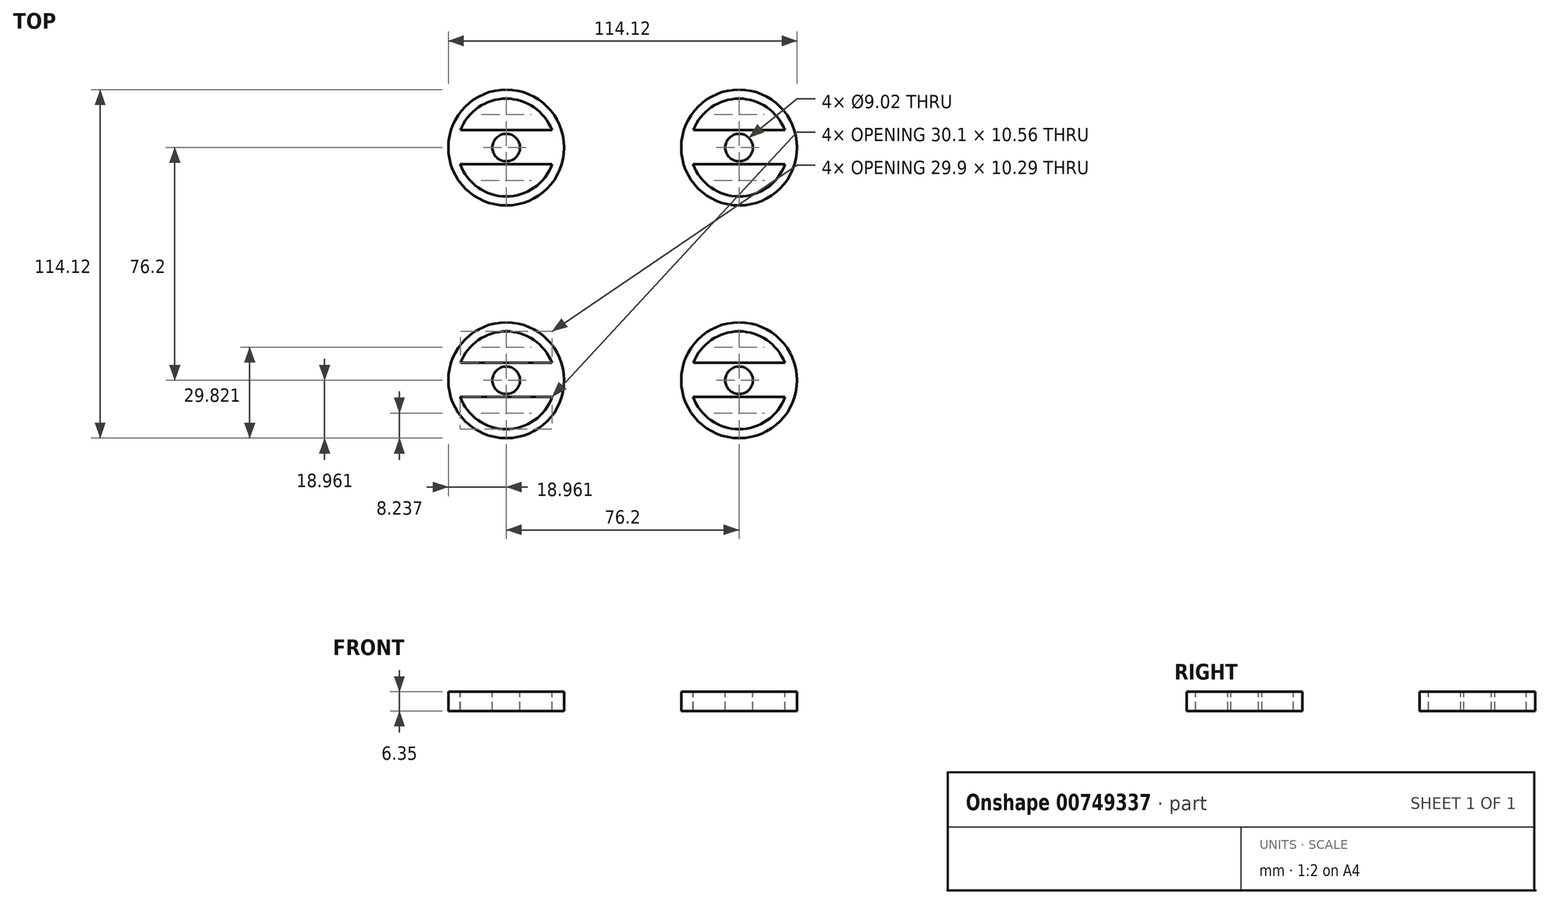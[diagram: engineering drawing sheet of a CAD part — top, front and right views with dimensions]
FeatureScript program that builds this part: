
annotation { "Feature Type Name" : "Feature", "Feature Type Description" : "" }
export const myFeature = defineFeature(function(context is Context, id is Id, definition is map)
    precondition{}
    {
        {
            var Q0;
            Q0=qCreatedBy(makeId("Top.planeOp"),FACE);
            var sketch = newSketch(context, id + "F0", { "sketchPlane" : qUnion([Q0])});
            skCircle(sketch, "E0", {"center": v(-43.12, 40.67) * mm, "radius": 18.96 * mm});
            skSolve(sketch);
        }
        {
            var Q0;
            Q0 = qSketchRegion(id + "F0", true);
            extrude(context, id + "F1", {"entities" : qUnion([Q0]), "depth" : 6.35 * mm, "offsetDistance" : 25.4 * mm});
        }
        {
            var Q0;
            Q0=makeQuery(id+"F1.opExtrude","CAP_FACE",FACE,{"disambiguationData":[OSD([sQuery(id+"F0.wireOp",EDGE,"E0")])],"isStart":false});
            var sketch = newSketch(context, id + "F2", { "sketchPlane" : qUnion([Q0])});
            skCircle(sketch, "E1", {"center": v(-43.12, 40.67) * mm, "radius": 16 * mm});
            skSolve(sketch);
        }
        {
            var Q0;
            Q0 = qSketchRegion(id + "F2", true);
            extrude(context, id + "F3", {"entities" : qUnion([Q0]), "operationType" : NewBodyOperationType.REMOVE, "oppositeDirection" : true, "depth" : 25.4 * mm, "offsetDistance" : 25.4 * mm});
        }
        {
            var Q0;
            Q0=makeQuery(id+"F1.opExtrude","CAP_FACE",FACE,{"disambiguationData":[OSD([sQuery(id+"F0.wireOp",EDGE,"E0")])],"isStart":false});
            var sketch = newSketch(context, id + "F4", { "sketchPlane" : qUnion([Q0])});
            skLineSegment(sketch, "E2.bottom", {"start": v(-60.69, 46.38) * mm, "end": v(-25.18, 46.38) * mm});
            skLineSegment(sketch, "E2.top", {"start": v(-60.69, 35.23) * mm, "end": v(-25.18, 35.23) * mm});
            skLineSegment(sketch, "E2.left", {"start": v(-60.69, 46.38) * mm, "end": v(-60.69, 35.23) * mm});
            skLineSegment(sketch, "E2.right", {"start": v(-25.18, 46.38) * mm, "end": v(-25.18, 35.23) * mm});
            skSolve(sketch);
        }
        {
            var Q0;
            Q0 = qSketchRegion(id + "F4", true);
            extrude(context, id + "F5", {"entities" : qUnion([Q0]), "operationType" : NewBodyOperationType.ADD, "oppositeDirection" : true, "depth" : 6.35 * mm, "offsetDistance" : 25.4 * mm});
        }
        {
            var Q0;
            Q0=makeQuery(id+"F5.boolean.opBoolean","MERGE",FACE,{"derivedFrom":[makeQuery(id+"F1.opExtrude","CAP_FACE",FACE,{"disambiguationData":[OSD([sQuery(id+"F0.wireOp",EDGE,"E0")])],"isStart":false}),makeQuery(id+"F5.opExtrude","CAP_FACE",FACE,{"disambiguationData":[OSD([sQuery(id+"F4.wireOp",EDGE,"E2.bottom"),sQuery(id+"F4.wireOp",EDGE,"E2.top"),sQuery(id+"F4.wireOp",EDGE,"E2.left"),sQuery(id+"F4.wireOp",EDGE,"E2.right")])],"isStart":true})]});
            var sketch = newSketch(context, id + "F6", { "sketchPlane" : qUnion([Q0])});
            skCircle(sketch, "E3", {"center": v(-43.12, 40.67) * mm, "radius": 4.5 * mm});
            skSolve(sketch);
        }
        {
            var Q0;
            Q0 = qSketchRegion(id + "F6", true);
            extrude(context, id + "F7", {"entities" : qUnion([Q0]), "operationType" : NewBodyOperationType.REMOVE, "oppositeDirection" : true, "depth" : 6.35 * mm, "offsetDistance" : 25.4 * mm});
        }
        {
            var Q0;
            Q0=makeQuery(id+"F1.opExtrude","SWEPT_BODY",BODY,{"disambiguationData":[OSD([sQuery(id+"F0.wireOp",EDGE,"E0")])]});
            transform(context, id + "F8", {"entities" : qUnion([Q0]), "transformType" : TransformType.TRANSLATION_3D, "dx" : 76.2 * mm, "dy" : 0 * mm, "dz" : 0 * mm, "makeCopy" : true});
        }
        {
            var Q0;
            Q0=makeQuery(id+"F8.opPattern","COPY",BODY,{"derivedFrom":makeQuery(id+"F1.opExtrude","SWEPT_BODY",BODY,{"disambiguationData":[OSD([sQuery(id+"F0.wireOp",EDGE,"E0")])]}),"instanceName":"1"});
            transform(context, id + "F9", {"entities" : qUnion([Q0]), "transformType" : TransformType.TRANSLATION_3D, "dx" : 0 * mm, "dy" : -76.2 * mm, "dz" : 0 * mm, "makeCopy" : true});
        }
        {
            var Q0;
            Q0=makeQuery(id+"F9.opPattern","COPY",BODY,{"derivedFrom":makeQuery(id+"F8.opPattern","COPY",BODY,{"derivedFrom":makeQuery(id+"F1.opExtrude","SWEPT_BODY",BODY,{"disambiguationData":[OSD([sQuery(id+"F0.wireOp",EDGE,"E0")])]}),"instanceName":"1"}),"instanceName":"1"});
            transform(context, id + "F10", {"entities" : qUnion([Q0]), "transformType" : TransformType.TRANSLATION_3D, "dx" : -76.2 * mm, "dy" : 0 * mm, "dz" : 0 * mm, "makeCopy" : true});
        }
    });
